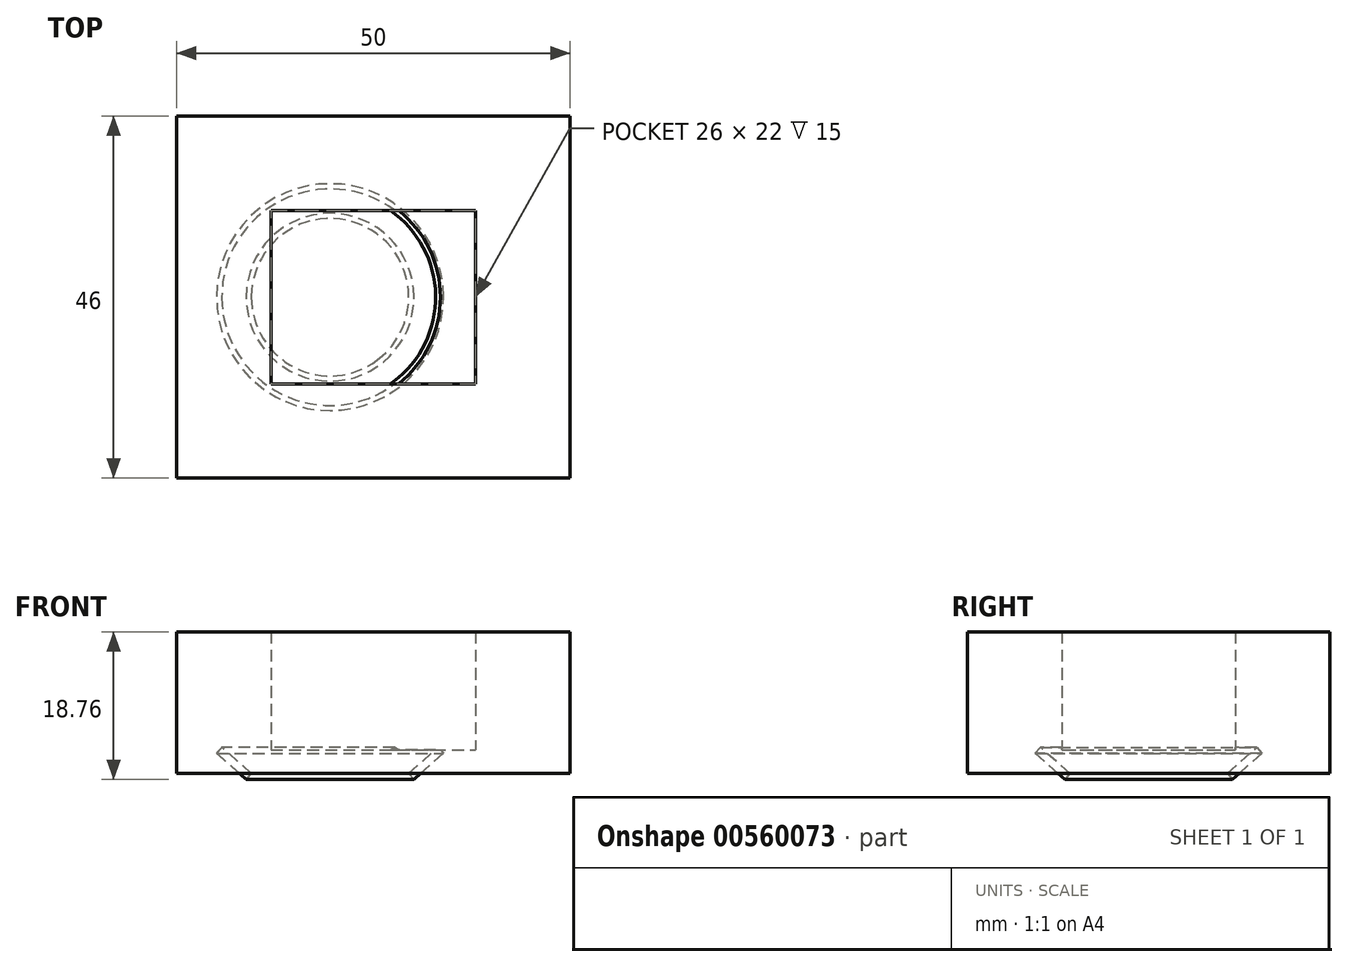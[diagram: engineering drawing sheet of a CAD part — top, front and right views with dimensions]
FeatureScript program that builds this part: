
annotation { "Feature Type Name" : "Feature", "Feature Type Description" : "" }
export const myFeature = defineFeature(function(context is Context, id is Id, definition is map)
    precondition{}
    {
        {
            var Q0;
            Q0=qCreatedBy(makeId("Front.planeOp"),FACE);
            var sketch = newSketch(context, id + "F0", { "sketchPlane" : qUnion([Q0])});
            skLineSegment(sketch, "E0", {"start": v(0, 0) * mm, "end": v(0, 28.5) * mm, "construction": true});
            skLineSegment(sketch, "E1", {"start": v(-10, -3) * mm, "end": v(-13.75, 0.3) * mm});
            skLineSegment(sketch, "E2", {"start": v(-13.75, 0.3) * mm, "end": v(-14.41, -0.45) * mm});
            skLineSegment(sketch, "E3", {"start": v(-14.41, -0.45) * mm, "end": v(-10.66, -3.76) * mm});
            skLineSegment(sketch, "E4", {"start": v(-10.66, -3.76) * mm, "end": v(-10, -3) * mm});
            skSolve(sketch);
        }
        {
            var Q0;
            Q0 = qSketchRegion(id + "F0", true);
            var Q1;
            Q1=sQuery(id+"F0.wireOp",EDGE,"E0");
            revolve(context, id + "F1", {"entities" : qUnion([Q0]), "axis" : qUnion([Q1]), "revolveType" : RevolveType.FULL});
        }
        {
            var Q0;
            Q0=qCreatedBy(makeId("Top.planeOp"),FACE);
            var sketch = newSketch(context, id + "F2", { "sketchPlane" : qUnion([Q0])});
            skLineSegment(sketch, "E5.bottom", {"start": v(-4.5, 8) * mm, "end": v(15.5, 8) * mm});
            skLineSegment(sketch, "E5.top", {"start": v(-4.5, -8) * mm, "end": v(15.5, -8) * mm});
            skLineSegment(sketch, "E5.left", {"start": v(-4.5, 8) * mm, "end": v(-4.5, -8) * mm});
            skLineSegment(sketch, "E5.right", {"start": v(15.5, 8) * mm, "end": v(15.5, -8) * mm});
            skSolve(sketch);
        }
        {
            var Q0;
            Q0=makeQuery(id+"F2.imprint","IMPRINT",FACE,{"disambiguationData":[TD([[makeQuery(id+"F2.imprint","IMPRINT",EDGE,{"derivedFrom":sQuery(id+"F2.wireOp",EDGE,"E5.bottom")}),-1.0]])]});
            extrude(context, id + "F3", {"entities" : qUnion([Q0]), "depth" : 11.5 * mm, "offsetDistance" : 25 * mm});
        }
        {
            var Q0;
            Q0=qCreatedBy(makeId("Top.planeOp"),FACE);
            var sketch = newSketch(context, id + "F4", { "sketchPlane" : qUnion([Q0])});
            skLineSegment(sketch, "E6.bottom", {"start": v(-19.5, 23) * mm, "end": v(30.5, 23) * mm});
            skLineSegment(sketch, "E6.top", {"start": v(-19.5, -23) * mm, "end": v(30.5, -23) * mm});
            skLineSegment(sketch, "E6.left", {"start": v(-19.5, 23) * mm, "end": v(-19.5, -23) * mm});
            skLineSegment(sketch, "E6.right", {"start": v(30.5, 23) * mm, "end": v(30.5, -23) * mm});
            skLineSegment(sketch, "E7.bottom", {"start": v(-7.5, -11) * mm, "end": v(18.5, -11) * mm});
            skLineSegment(sketch, "E7.top", {"start": v(-7.5, 11) * mm, "end": v(18.5, 11) * mm});
            skLineSegment(sketch, "E7.left", {"start": v(-7.5, -11) * mm, "end": v(-7.5, 11) * mm});
            skLineSegment(sketch, "E7.right", {"start": v(18.5, -11) * mm, "end": v(18.5, 11) * mm});
            skSolve(sketch);
        }
        {
            var Q0;
            Q0=makeQuery(id+"F4.imprint","IMPRINT",FACE,{"disambiguationData":[TD([[makeQuery(id+"F4.imprint","IMPRINT",EDGE,{"derivedFrom":sQuery(id+"F4.wireOp",EDGE,"E6.bottom")}),-1.0]])]});
            var Q1;
            Q1=makeQuery(id+"F4.imprint","IMPRINT",FACE,{"disambiguationData":[TD([[makeQuery(id+"F4.imprint","IMPRINT",EDGE,{"derivedFrom":sQuery(id+"F4.wireOp",EDGE,"E7.bottom")}),1.0]])]});
            extrude(context, id + "F5", {"entities" : qUnion([Q0, Q1]), "depth" : 15 * mm, "offsetDistance" : 25 * mm, "hasSecondDirection" : true, "secondDirectionOppositeDirection" : true, "secondDirectionDepth" : 3 * mm});
        }
        {
            var Q0;
            Q0=makeQuery(id+"F4.imprint","IMPRINT",FACE,{"disambiguationData":[TD([[makeQuery(id+"F4.imprint","IMPRINT",EDGE,{"derivedFrom":sQuery(id+"F4.wireOp",EDGE,"E7.bottom")}),1.0]])]});
            extrude(context, id + "F6", {"entities" : qUnion([Q0]), "operationType" : NewBodyOperationType.REMOVE, "depth" : 25 * mm, "offsetDistance" : 25 * mm});
        }
    });
